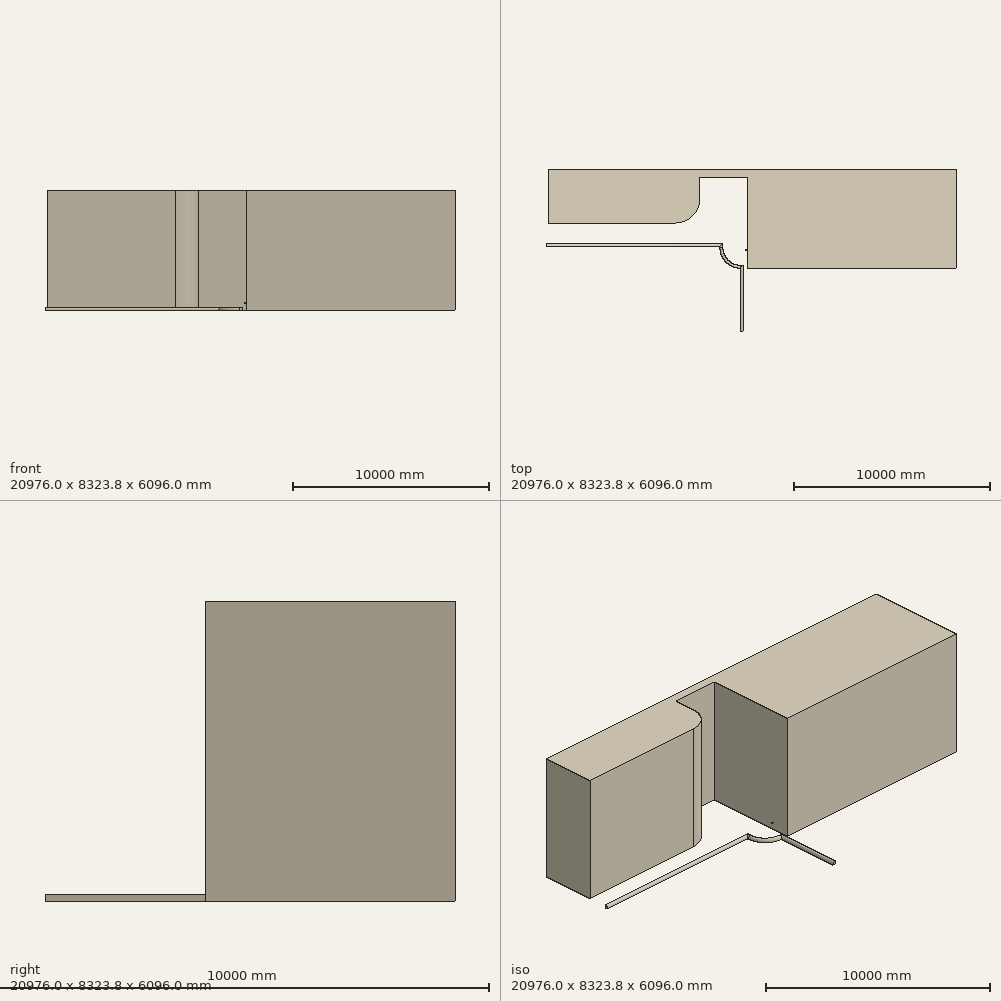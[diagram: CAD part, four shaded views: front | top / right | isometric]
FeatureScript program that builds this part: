
annotation { "Feature Type Name" : "Feature", "Feature Type Description" : "" }
export const myFeature = defineFeature(function(context is Context, id is Id, definition is map)
    precondition{}
    {
        {
            var Q0;
            Q0=qCreatedBy(makeId("Top.planeOp"),FACE);
            var sketch = newSketch(context, id + "F7", { "sketchPlane" : qUnion([Q0])});
            skLineSegment(sketch, "E0", {"start": v(-7759.81, 0) * mm, "end": v(0, 0) * mm});
            skLineSegment(sketch, "E1", {"start": v(0, 2308.06) * mm, "end": v(2438.4, 2308.06) * mm});
            skLineSegment(sketch, "E2", {"start": v(2438.4, 2308.06) * mm, "end": v(2438.4, -2310.78) * mm});
            skLineSegment(sketch, "E3", {"start": v(2438.4, -2310.78) * mm, "end": v(13126.7, -2310.78) * mm});
            skLineSegment(sketch, "E4", {"start": v(0, 2308.06) * mm, "end": v(0, 0) * mm});
            skLineSegment(sketch, "E5", {"start": v(-7849.32, -1044.65) * mm, "end": v(1180.88, -1044.65) * mm});
            skLineSegment(sketch, "E6", {"start": v(1180.88, -1044.65) * mm, "end": v(1180.88, -1244.17) * mm});
            skLineSegment(sketch, "E7", {"start": v(2095.28, -2158.57) * mm, "end": v(2221.43, -2158.57) * mm});
            skLineSegment(sketch, "E8", {"start": v(2221.43, -2158.57) * mm, "end": v(2221.43, -5567.8) * mm});
            skLineSegment(sketch, "E9", {"start": v(-7759.81, 0) * mm, "end": v(-7759.81, 2756) * mm});
            skLineSegment(sketch, "E10", {"start": v(-7759.81, 2756) * mm, "end": v(13126.7, 2756) * mm});
            skLineSegment(sketch, "E11", {"start": v(13126.7, 2756) * mm, "end": v(13126.7, -2310.78) * mm});
            skPoint(sketch, "E12.visualSharp", {"position": v(1180.88, -2158.57) * mm});
            skArc(sketch, "E12.filletArc", {"start": v(1180.88, -1244.17) * mm, "mid": v(1448.7, -1890.75) * mm, "end": v(2095.28, -2158.57) * mm});
            skSolve(sketch);
        }
        {
            var Q0;
            Q0=makeQuery(id+"F7.imprint","IMPRINT",FACE,{"disambiguationData":[TD([[makeQuery(id+"F7.imprint","IMPRINT",EDGE,{"derivedFrom":sQuery(id+"F7.wireOp",EDGE,"E0")}),1.0]])]});
            extrude(context, id + "F0", {"entities" : qUnion([Q0]), "depth" : 6096 * mm});
        }
        {
            var Q0;
            Q0=sQuery(id+"F7.wireOp",VERTEX,"E5.start");
            var Q1;
            Q1=sQuery(id+"F7.wireOp",EDGE,"E5");
            cPlane(context, id + "F1", {"entities" : qUnion([Q0, Q1]), "cplaneType" : CPlaneType.LINE_POINT, "offset" : 25 * mm, "width" : 150 * mm, "height" : 150 * mm});
        }
        {
            var Q0;
            Q0=qCreatedBy(id+"F1.planeOp",FACE);
            var sketch = newSketch(context, id + "F2", { "sketchPlane" : qUnion([Q0])});
            skLineSegment(sketch, "E13", {"start": v(-1054.93, 0) * mm, "end": v(-1054.93, 149.56) * mm});
            skLineSegment(sketch, "E14", {"start": v(-1054.93, 0) * mm, "end": v(-1204.49, 0) * mm});
            skArc(sketch, "E15", {"start": v(-1054.93, 149.56) * mm, "mid": v(-1160.68, 105.76) * mm, "end": v(-1204.49, 0) * mm});
            skSolve(sketch);
        }
        {
            var Q0;
            Q0 = qSketchRegion(id + "F2", true);
            var Q1;
            Q1 = qConstructionFilter(qBodyType(qCreatedBy(id + "F2" ,EDGE), BodyType.WIRE), ConstructionObject.NO);
            var Q2;
            Q2=sQuery(id+"F7.wireOp",EDGE,"E5");
            var Q3;
            Q3=sQuery(id+"F7.wireOp",EDGE,"E6");
            var Q4;
            Q4=sQuery(id+"F7.wireOp",EDGE,"E12.filletArc");
            var Q5;
            Q5=sQuery(id+"F7.wireOp",EDGE,"E7");
            var Q6;
            Q6=sQuery(id+"F7.wireOp",EDGE,"E8");
            sweep(context, id + "F3", {"profiles" : qUnion([Q0]), "surfaceProfiles" : qUnion([Q1]), "path" : qUnion([Q2, Q3, Q4, Q5, Q6])});
        }
        {
            var Q0;
            Q0=makeQuery(id+"F0.opExtrude","SWEPT_FACE",FACE,{"disambiguationData":[OSD([sQuery(id+"F7.wireOp",EDGE,"E2")])]});
            var sketch = newSketch(context, id + "F4", { "sketchPlane" : qUnion([Q0])});
            skCircle(sketch, "E16", {"center": v(1402.42, 340.92) * mm, "radius": 25.4 * mm});
            skSolve(sketch);
        }
        {
            var Q0;
            Q0 = qSketchRegion(id + "F4", true);
            extrude(context, id + "F5", {"entities" : qUnion([Q0]), "depth" : 101.6 * mm});
        }
        {
            var Q0;
            Q0=makeQuery(id+"F0.opExtrude","SWEPT_EDGE",EDGE,{"disambiguationData":[OSD([sQuery(id+"F7.wireOp",EDGE,"E0"),sQuery(id+"F7.wireOp",EDGE,"E4")])]});
            fillet(context, id + "F6", {"entities" : qUnion([Q0]), "radius" : 1219.2 * mm, "tangentPropagation" : true, "allowEdgeOverflow" : false});
        }
    });
